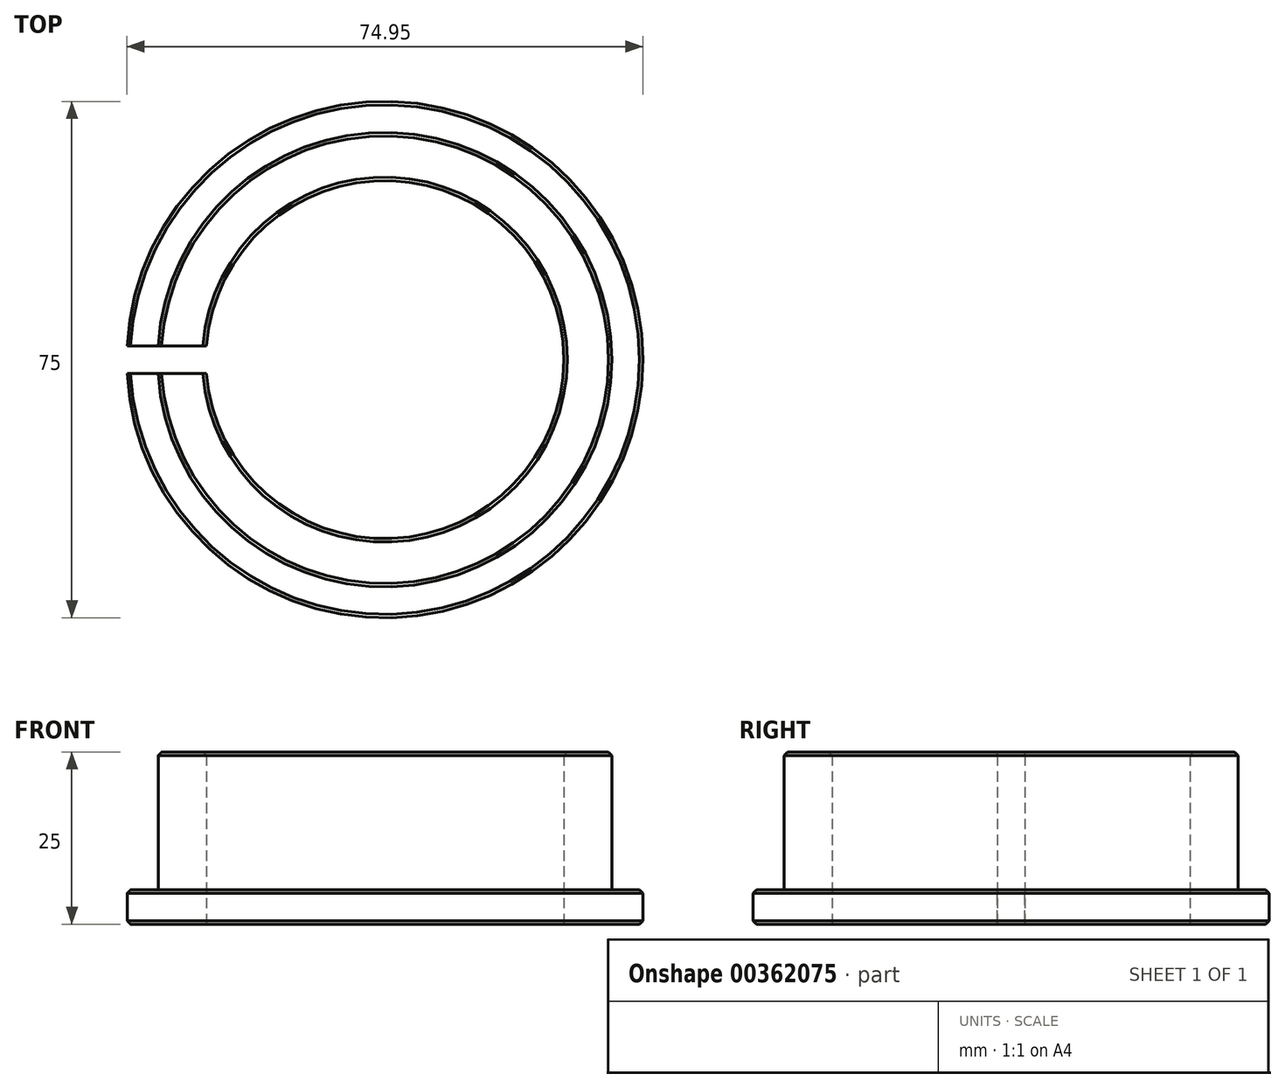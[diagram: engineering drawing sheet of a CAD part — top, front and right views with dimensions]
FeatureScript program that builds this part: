
annotation { "Feature Type Name" : "Feature", "Feature Type Description" : "" }
export const myFeature = defineFeature(function(context is Context, id is Id, definition is map)
    precondition{}
    {
        {
            var Q0;
            Q0=qCreatedBy(makeId("Top.planeOp"),FACE);
            var sketch = newSketch(context, id + "F0", { "sketchPlane" : qUnion([Q0])});
            skCircle(sketch, "E0", {"center": v(0, 0) * mm, "radius": 26 * mm});
            skCircle(sketch, "E1", {"center": v(0, 0) * mm, "radius": 33 * mm});
            skSolve(sketch);
        }
        {
            var Q0;
            Q0 = qSketchRegion(id + "F0", true);
            extrude(context, id + "F1", {"entities" : qUnion([Q0]), "depth" : 20 * mm});
        }
        {
            var Q0;
            Q0=qCreatedBy(makeId("Top.planeOp"),FACE);
            var sketch = newSketch(context, id + "F2", { "sketchPlane" : qUnion([Q0])});
            skCircle(sketch, "E2", {"center": v(0, 0) * mm, "radius": 26 * mm});
            skCircle(sketch, "E3", {"center": v(0, 0) * mm, "radius": 37.5 * mm});
            skSolve(sketch);
        }
        {
            var Q0;
            Q0 = qSketchRegion(id + "F2", true);
            extrude(context, id + "F3", {"entities" : qUnion([Q0]), "operationType" : NewBodyOperationType.ADD, "oppositeDirection" : true, "depth" : 5 * mm});
        }
        {
            var Q0;
            Q0=qCreatedBy(makeId("Top.planeOp"),FACE);
            var sketch = newSketch(context, id + "F4", { "sketchPlane" : qUnion([Q0])});
            skLineSegment(sketch, "E4.bottom", {"start": v(-42.95, -2) * mm, "end": v(-20.95, -2) * mm});
            skLineSegment(sketch, "E4.top", {"start": v(-42.95, 2) * mm, "end": v(-20.95, 2) * mm});
            skLineSegment(sketch, "E4.left", {"start": v(-42.95, -2) * mm, "end": v(-42.95, 2) * mm});
            skLineSegment(sketch, "E4.right", {"start": v(-20.95, -2) * mm, "end": v(-20.95, 2) * mm});
            skPoint(sketch, "E4.middle", {"position": v(-31.95, 0) * mm});
            skSolve(sketch);
        }
        {
            var Q0;
            Q0 = qSketchRegion(id + "F4", true);
            extrude(context, id + "F5", {"entities" : qUnion([Q0]), "operationType" : NewBodyOperationType.REMOVE, "endBound" : BoundingType.SYMMETRIC, "oppositeDirection" : true, "depth" : 50 * mm});
        }
        {
            var Q0;
            Q0=makeQuery(id+"F1.opExtrude","CAP_EDGE",EDGE,{"disambiguationData":[OSD([sQuery(id+"F0.wireOp",EDGE,"E1")])],"isStart":false});
            var Q1;
            Q1=makeQuery(id+"F1.opExtrude","CAP_EDGE",EDGE,{"disambiguationData":[OSD([sQuery(id+"F0.wireOp",EDGE,"E0")])],"isStart":false});
            var Q2;
            Q2=makeQuery(id+"F3.opExtrude","CAP_EDGE",EDGE,{"disambiguationData":[OSD([sQuery(id+"F2.wireOp",EDGE,"E3")])],"isStart":true});
            var Q3;
            Q3=makeQuery(id+"F3.opExtrude","CAP_EDGE",EDGE,{"disambiguationData":[OSD([sQuery(id+"F2.wireOp",EDGE,"E3")])],"isStart":false});
            chamfer(context, id + "F6", {"entities" : qUnion([Q0, Q1, Q2, Q3]), "width" : .5 * mm, "tangentPropagation" : true});
        }
    });
